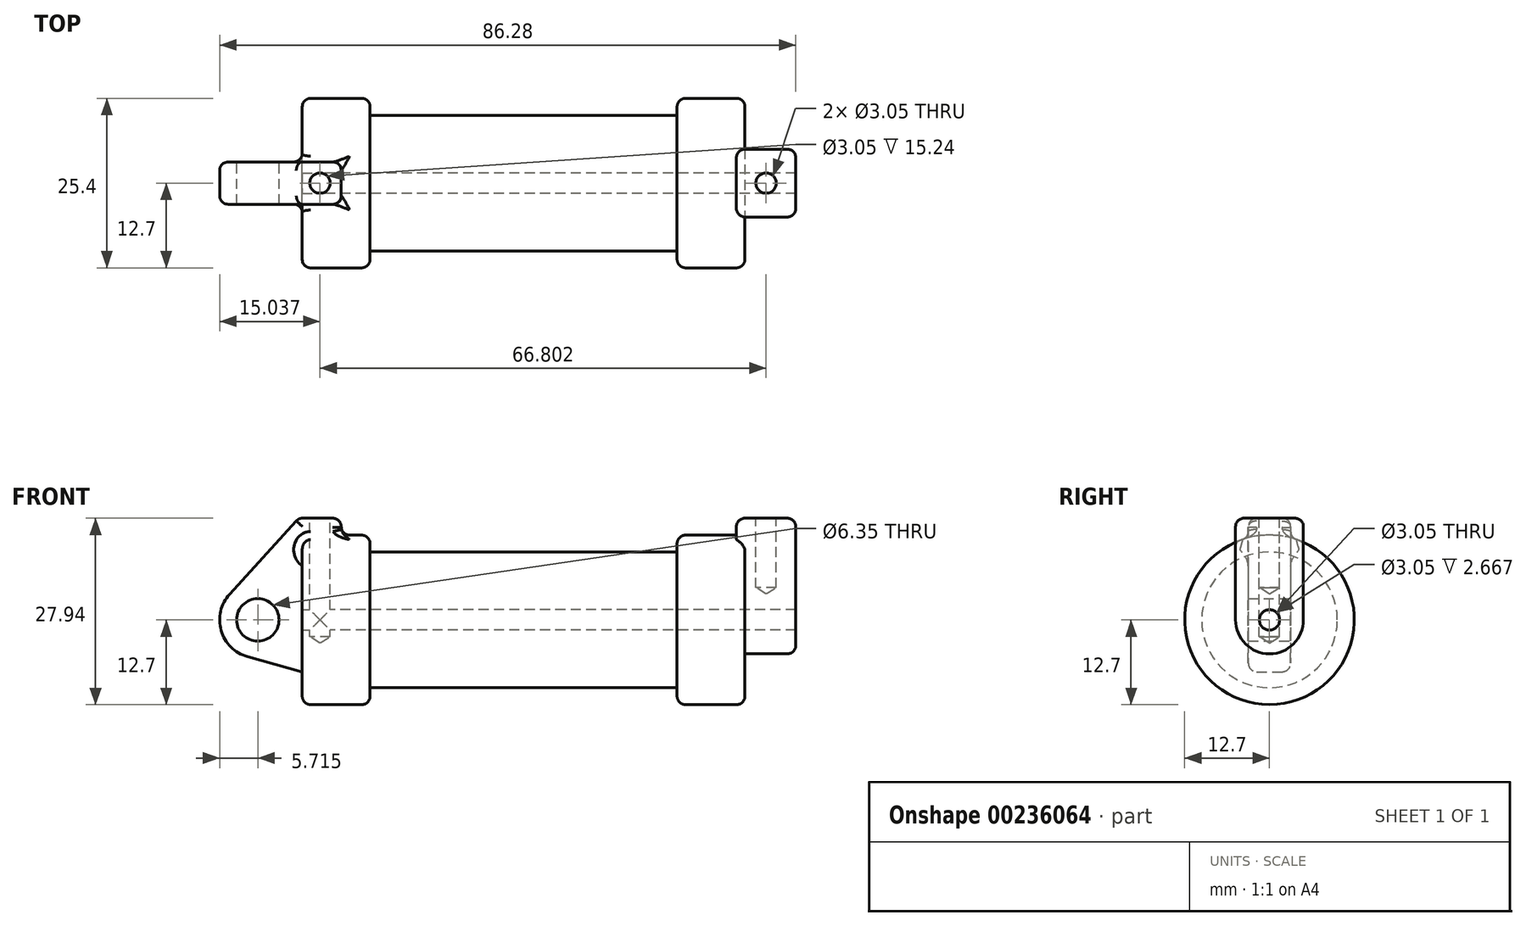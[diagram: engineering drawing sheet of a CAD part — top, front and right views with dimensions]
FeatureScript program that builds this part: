
annotation { "Feature Type Name" : "Feature", "Feature Type Description" : "" }
export const myFeature = defineFeature(function(context is Context, id is Id, definition is map)
    precondition{}
    {
        {
            var Q0;
            Q0=qCreatedBy(makeId("Front.planeOp"),FACE);
            var sketch = newSketch(context, id + "F0", { "sketchPlane" : qUnion([Q0])});
            skLineSegment(sketch, "E0", {"start": v(0, 0) * mm, "end": v(0, 12.7) * mm});
            skLineSegment(sketch, "E1", {"start": v(0, 12.7) * mm, "end": v(10.16, 12.7) * mm});
            skLineSegment(sketch, "E2", {"start": v(10.16, 12.7) * mm, "end": v(10.16, 10.16) * mm});
            skLineSegment(sketch, "E3", {"start": v(10.16, 10.16) * mm, "end": v(56.13, 10.16) * mm});
            skLineSegment(sketch, "E4", {"start": v(56.13, 10.16) * mm, "end": v(56.13, 12.7) * mm});
            skLineSegment(sketch, "E5", {"start": v(56.13, 12.7) * mm, "end": v(66.3, 12.7) * mm});
            skLineSegment(sketch, "E6", {"start": v(66.3, 12.7) * mm, "end": v(66.3, 0) * mm});
            skLineSegment(sketch, "E7", {"start": v(66.3, 0) * mm, "end": v(0, 0) * mm});
            skLineSegment(sketch, "E8", {"start": v(5.84, 15.24) * mm, "end": v(-0.5, 15.24) * mm});
            skLineSegment(sketch, "E9", {"start": v(-0.5, 15.24) * mm, "end": v(-10.88, 3.85) * mm});
            skLineSegment(sketch, "E10", {"start": v(0, 0) * mm, "end": v(-6.65, 0) * mm});
            skCircle(sketch, "E11", {"center": v(-6.65, 0) * mm, "radius": 5.72 * mm});
            skCircle(sketch, "E12", {"center": v(-6.65, 0) * mm, "radius": 3.18 * mm});
            skLineSegment(sketch, "E13", {"start": v(5.84, 15.24) * mm, "end": v(5.84, -9.4) * mm});
            skLineSegment(sketch, "E14", {"start": v(5.84, -9.4) * mm, "end": v(-8.18, -5.5) * mm});
            skSolve(sketch);
        }
        {
            var Q0;
            {var subQ4=sQuery(id+"F0.wireOp",EDGE,"E0");Q0=makeQuery(id+"F0.imprint","IMPRINT",FACE,{"disambiguationData":[TD([[makeQuery(id+"F0.imprint","IMPRINT",EDGE,{"derivedFrom":subQ4}),-1.0]])]});}
            var Q1;
            {var subQ0=sQuery(id+"F0.wireOp",EDGE,"E2");Q1=makeQuery(id+"F0.imprint","IMPRINT",FACE,{"disambiguationData":[TD([[makeQuery(id+"F0.imprint","IMPRINT",EDGE,{"derivedFrom":subQ0}),-1.0]])]});}
            var Q2;
            Q2=sQuery(id+"F0.wireOp",EDGE,"E7");
            revolve(context, id + "F1", {"entities" : qUnion([Q0, Q1]), "axis" : qUnion([Q2]), "revolveType" : RevolveType.FULL});
        }
        {
            var Q0;
            {var subQ3=sQuery(id+"F0.wireOp",EDGE,"yhVQYzbj-QzQz-IxGe-JuAQ-agU5pRzT5Fz5");Q0=makeQuery(id+"F0.imprint","IMPRINT",FACE,{"disambiguationData":[TD([[makeQuery(id+"F0.imprint","IMPRINT",EDGE,{"derivedFrom":subQ3}),1.0]])]});}
            var Q1;
            {var subQ6=sQuery(id+"F0.wireOp",EDGE,"E0");Q1=makeQuery(id+"F0.imprint","IMPRINT",FACE,{"disambiguationData":[TD([[makeQuery(id+"F0.imprint","IMPRINT",EDGE,{"derivedFrom":subQ6}),1.0]])]});}
            var Q2;
            {var subQ0=sQuery(id+"F0.wireOp",EDGE,"E14");Q2=makeQuery(id+"F0.imprint","IMPRINT",FACE,{"disambiguationData":[TD([[makeQuery(id+"F0.imprint","IMPRINT",EDGE,{"derivedFrom":subQ0}),-1.0]])]});}
            var Q3;
            {var subQ4=sQuery(id+"F0.wireOp",EDGE,"E12");Q3=makeQuery(id+"F0.imprint","IMPRINT",FACE,{"disambiguationData":[TD([[makeQuery(id+"F0.imprint","IMPRINT",EDGE,{"derivedFrom":subQ4}),-1.0]])]});}
            var Q4;
            {var subQ4=sQuery(id+"F0.wireOp",EDGE,"E0");Q4=makeQuery(id+"F0.imprint","IMPRINT",FACE,{"disambiguationData":[TD([[makeQuery(id+"F0.imprint","IMPRINT",EDGE,{"derivedFrom":subQ4}),-1.0]])]});}
            extrude(context, id + "F2", {"entities" : qUnion([Q0, Q1, Q2, Q3, Q4]), "operationType" : NewBodyOperationType.ADD, "endBound" : BoundingType.SYMMETRIC, "depth" : 6.35 * mm});
        }
        {
            var Q0;
            Q0=makeQuery(id+"F1.opRevolve","SWEPT_FACE",FACE,{"disambiguationData":[OSD([sQuery(id+"F0.wireOp",EDGE,"E6")])]});
            var sketch = newSketch(context, id + "F3", { "sketchPlane" : qUnion([Q0])});
            skCircle(sketch, "E15", {"center": v(0, 0) * mm, "radius": 1.52 * mm});
            skCircle(sketch, "E16", {"center": v(0, 0) * mm, "radius": 5.08 * mm});
            skLineSegment(sketch, "E17", {"start": v(5.08, 0) * mm, "end": v(5.08, 15.24) * mm});
            skLineSegment(sketch, "E18", {"start": v(-5.08, 0) * mm, "end": v(-5.08, 15.24) * mm});
            skLineSegment(sketch, "E19", {"start": v(-5.08, 15.24) * mm, "end": v(5.08, 15.24) * mm});
            skSolve(sketch);
        }
        {
            var Q0;
            Q0 = qSketchRegion(id + "F3", true);
            extrude(context, id + "F4", {"entities" : qUnion([Q0]), "operationType" : NewBodyOperationType.ADD, "depth" : 7.62 * mm, "hasSecondDirection" : true, "secondDirectionOppositeDirection" : true, "secondDirectionDepth" : 1.27 * mm});
        }
        {
            var Q0;
            Q0=makeQuery(id+"F2.opExtrude","SWEPT_FACE",FACE,{"disambiguationData":[OSD([sQuery(id+"F0.wireOp",EDGE,"E8")])]});
            var sketch = newSketch(context, id + "F5", { "sketchPlane" : qUnion([Q0])});
            skLineSegment(sketch, "E20", {"start": v(-0.5, 3.18) * mm, "end": v(5.84, -3.18) * mm});
            skLineSegment(sketch, "E21", {"start": v(5.84, 3.18) * mm, "end": v(-0.5, -3.18) * mm});
            skPoint(sketch, "E22", {"position": v(2.67, 0) * mm});
            skLineSegment(sketch, "E23", {"start": v(65.1, 4.94) * mm, "end": v(73.65, -4.88) * mm});
            skLineSegment(sketch, "E24", {"start": v(73.83, 5.15) * mm, "end": v(65.14, -5.18) * mm});
            skPoint(sketch, "E25", {"position": v(69.45, -0.06) * mm});
            skSolve(sketch);
        }
        {
            var Q0;
            Q0=sQuery(id+"F5.wireOp",VERTEX,"E22");
            var Q1;
            Q1=makeQuery(id+"F1.opRevolve","SWEPT_BODY",BODY,{"disambiguationData":[OSD([sQuery(id+"F0.wireOp",EDGE,"E0"),sQuery(id+"F0.wireOp",EDGE,"E1"),sQuery(id+"F0.wireOp",EDGE,"E2"),sQuery(id+"F0.wireOp",EDGE,"E3"),sQuery(id+"F0.wireOp",EDGE,"E4"),sQuery(id+"F0.wireOp",EDGE,"E5"),sQuery(id+"F0.wireOp",EDGE,"E6"),sQuery(id+"F0.wireOp",EDGE,"E7")])]});
            hole(context, id + "F6", {"style" : HoleStyle.SIMPLE, "endStyle" : HoleEndStyle.BLIND, "holeDiameter" : 3.05 * mm, "holeDepth" : 17.78 * mm, "startFromSketch" : true, "locations" : qUnion([Q0]), "scope" : qUnion([Q1])});
        }
        {
            var Q0;
            Q0=makeQuery(id+"F4.opExtrude","SWEPT_FACE",FACE,{"disambiguationData":[OSD([sQuery(id+"F3.wireOp",EDGE,"E19")])]});
            var sketch = newSketch(context, id + "F7", { "sketchPlane" : qUnion([Q0])});
            skLineSegment(sketch, "E26", {"start": v(65.02, 5.08) * mm, "end": v(73.91, -5.08) * mm});
            skLineSegment(sketch, "E27", {"start": v(73.91, 5.08) * mm, "end": v(65.02, -5.08) * mm});
            skPoint(sketch, "E28", {"position": v(69.47, 0) * mm});
            skSolve(sketch);
        }
        {
            var Q0;
            Q0=sQuery(id+"F7.wireOp",VERTEX,"E28");
            var Q1;
            Q1=makeQuery(id+"F1.opRevolve","SWEPT_BODY",BODY,{"disambiguationData":[OSD([sQuery(id+"F0.wireOp",EDGE,"E0"),sQuery(id+"F0.wireOp",EDGE,"E1"),sQuery(id+"F0.wireOp",EDGE,"E2"),sQuery(id+"F0.wireOp",EDGE,"E3"),sQuery(id+"F0.wireOp",EDGE,"E4"),sQuery(id+"F0.wireOp",EDGE,"E5"),sQuery(id+"F0.wireOp",EDGE,"E6"),sQuery(id+"F0.wireOp",EDGE,"E7")])]});
            hole(context, id + "F8", {"style" : HoleStyle.SIMPLE, "endStyle" : HoleEndStyle.BLIND, "holeDiameter" : 3.05 * mm, "holeDepth" : 10.4 * mm, "startFromSketch" : true, "locations" : qUnion([Q0]), "scope" : qUnion([Q1])});
        }
        {
            var Q0;
            Q0=makeQuery(id+"F4.boolean.opBoolean","SPLIT",FACE,{"disambiguationData":[TD([makeQuery(id+"F4.opExtrude","SWEPT_FACE",FACE,{"disambiguationData":[OSD([sQuery(id+"F3.wireOp",EDGE,"E15")])]})])],"derivedFrom":makeQuery(id+"F1.opRevolve","SWEPT_FACE",FACE,{"disambiguationData":[OSD([sQuery(id+"F0.wireOp",EDGE,"E6")])]})});
            var Q1;
            Q1=makeQuery(id+"F1.opRevolve","SWEPT_FACE",FACE,{"disambiguationData":[OSD([sQuery(id+"F0.wireOp",EDGE,"E0")])]});
            extrude(context, id + "F9", {"entities" : qUnion([Q0]), "operationType" : NewBodyOperationType.REMOVE, "endBound" : BoundingType.UP_TO_SURFACE, "oppositeDirection" : true, "endBoundEntityFace" : qUnion([Q1]), "depth" : 46.74 * mm});
        }
        {
            var Q0;
            Q0=makeQuery(id+"F1.opRevolve","SWEPT_FACE",FACE,{"disambiguationData":[OSD([sQuery(id+"F0.wireOp",EDGE,"E1")])]});
            fillet(context, id + "F10", {"entities" : qUnion([Q0]), "radius" : 1.27 * mm, "tangentPropagation" : true, "allowEdgeOverflow" : false});
        }
        {
            var Q0;
            Q0=makeQuery(id+"F2.opExtrude","SWEPT_FACE",FACE,{"disambiguationData":[OSD([sQuery(id+"F0.wireOp",EDGE,"E9")])]});
            fillet(context, id + "F11", {"entities" : qUnion([Q0]), "radius" : 1.27 * mm, "tangentPropagation" : true, "allowEdgeOverflow" : false});
        }
        {
            var Q0;
            Q0=makeQuery(id+"F2.opExtrude","CAP_EDGE",EDGE,{"disambiguationData":[OSD([sQuery(id+"F0.wireOp",EDGE,"E8")])],"isStart":false});
            fillet(context, id + "F12", {"entities" : qUnion([Q0]), "radius" : 1.27 * mm, "tangentPropagation" : true, "allowEdgeOverflow" : false});
        }
        {
            var Q0;
            Q0=makeQuery(id+"F2.opExtrude","CAP_EDGE",EDGE,{"disambiguationData":[OSD([sQuery(id+"F0.wireOp",EDGE,"E8")])],"isStart":true});
            fillet(context, id + "F13", {"entities" : qUnion([Q0]), "radius" : 1.27 * mm, "tangentPropagation" : true, "allowEdgeOverflow" : false});
        }
        {
            var Q0;
            Q0=makeQuery(id+"F2.opExtrude","SWEPT_EDGE",EDGE,{"disambiguationData":[OSD([sQuery(id+"F0.wireOp",EDGE,"E8"),sQuery(id+"F0.wireOp",EDGE,"E13")])]});
            fillet(context, id + "F14", {"entities" : qUnion([Q0]), "radius" : 1.27 * mm, "tangentPropagation" : true, "allowEdgeOverflow" : false});
        }
        {
            var Q0;
            Q0=makeQuery(id+"F1.opRevolve","SWEPT_EDGE",EDGE,{"disambiguationData":[OSD([sQuery(id+"F0.wireOp",EDGE,"E5"),sQuery(id+"F0.wireOp",EDGE,"E6")])]});
            fillet(context, id + "F15", {"entities" : qUnion([Q0]), "radius" : 1.27 * mm, "tangentPropagation" : true, "allowEdgeOverflow" : false});
        }
        {
            var Q0;
            Q0=makeQuery(id+"F4.opExtrude","CAP_EDGE",EDGE,{"disambiguationData":[OSD([sQuery(id+"F3.wireOp",EDGE,"E17")])],"isStart":false});
            fillet(context, id + "F16", {"entities" : qUnion([Q0]), "radius" : 1.27 * mm, "tangentPropagation" : true, "allowEdgeOverflow" : false});
        }
        {
            var Q0;
            Q0=makeQuery(id+"F4.opExtrude","SWEPT_EDGE",EDGE,{"disambiguationData":[OSD([sQuery(id+"F3.wireOp",EDGE,"E17"),sQuery(id+"F3.wireOp",EDGE,"E19")])]});
            fillet(context, id + "F17", {"entities" : qUnion([Q0]), "radius" : 1.27 * mm, "tangentPropagation" : true, "allowEdgeOverflow" : false});
        }
        {
            var Q0;
            Q0=makeQuery(id+"F4.opExtrude","CAP_EDGE",EDGE,{"disambiguationData":[OSD([sQuery(id+"F3.wireOp",EDGE,"E19")])],"isStart":true});
            fillet(context, id + "F18", {"entities" : qUnion([Q0]), "radius" : 1.27 * mm, "tangentPropagation" : true, "allowEdgeOverflow" : false});
        }
        {
            var Q0;
            Q0=makeQuery(id+"F1.opRevolve","SWEPT_EDGE",EDGE,{"disambiguationData":[OSD([sQuery(id+"F0.wireOp",EDGE,"E4"),sQuery(id+"F0.wireOp",EDGE,"E5")])]});
            fillet(context, id + "F19", {"entities" : qUnion([Q0]), "radius" : 1.27 * mm, "tangentPropagation" : true, "allowEdgeOverflow" : false});
        }
    });
